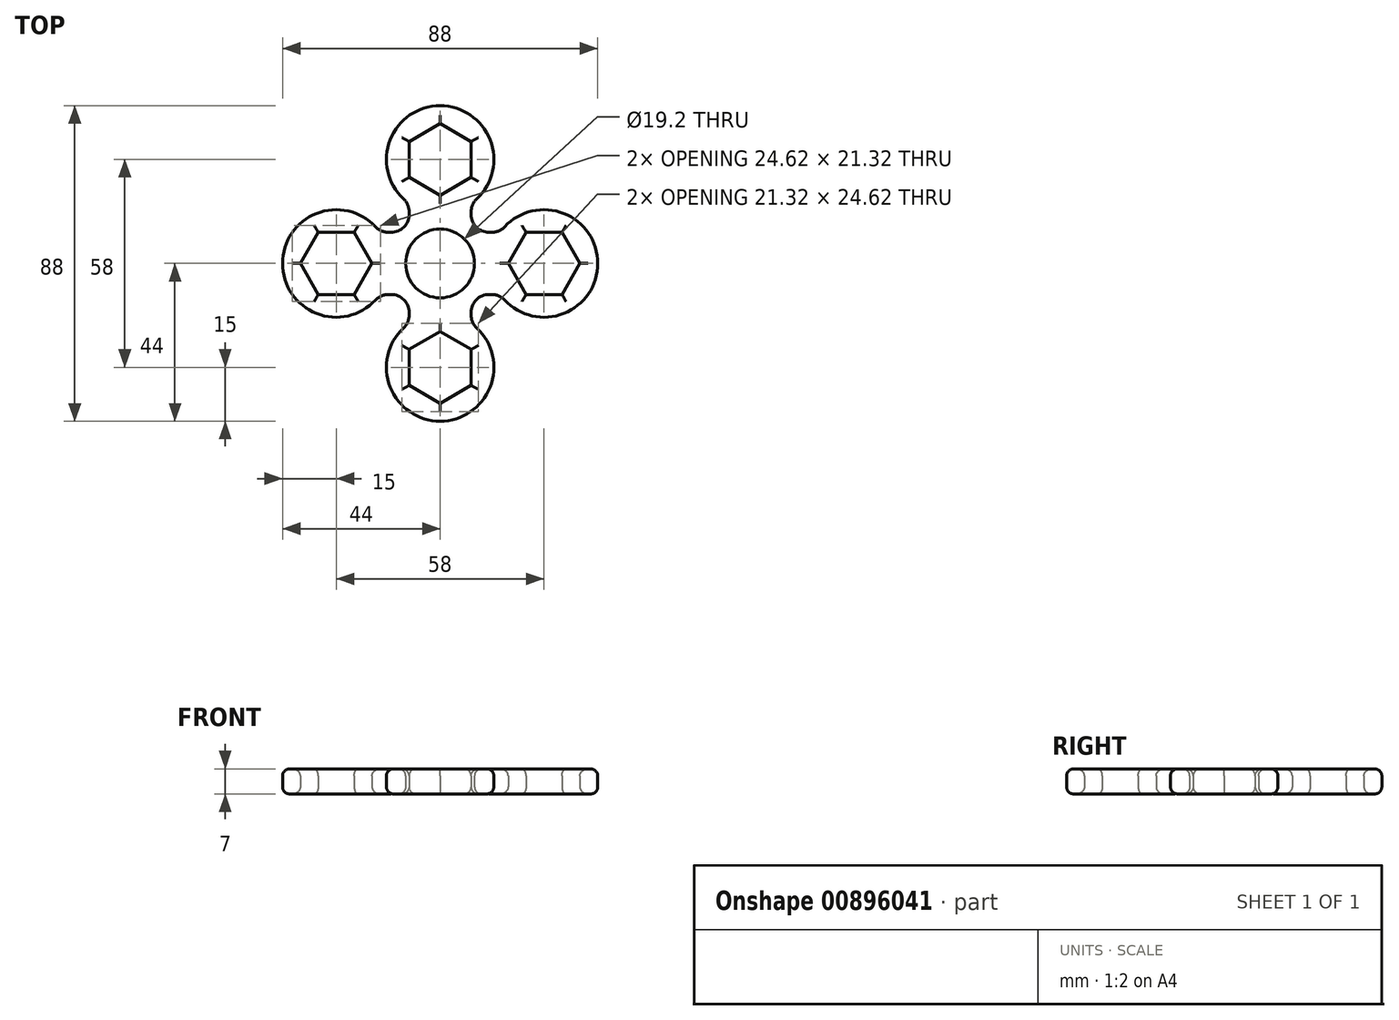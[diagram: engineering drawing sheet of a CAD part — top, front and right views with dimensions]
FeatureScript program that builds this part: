
annotation { "Feature Type Name" : "Feature", "Feature Type Description" : "" }
export const myFeature = defineFeature(function(context is Context, id is Id, definition is map)
    precondition{}
    {
        {
            var Q0;
            Q0=qCreatedBy(makeId("Top.planeOp"),FACE);
            var sketch = newSketch(context, id + "F0", { "sketchPlane" : qUnion([Q0])});
            skCircle(sketch, "E0", {"center": v(0, 0) * mm, "radius": 9.6 * mm});
            skLineSegment(sketch, "E1", {"start": v(0, 8.66) * mm, "end": v(0, 9.6) * mm, "construction": true});
            skLineSegment(sketch, "E2", {"start": v(0, -8.66) * mm, "end": v(0, -9.6) * mm});
            skCircle(sketch, "E3.cCircle", {"center": v(0, 29) * mm, "radius": 8.66 * mm, "construction": true});
            skLineSegment(sketch, "E3.0", {"start": v(8.66, 34) * mm, "end": v(8.66, 24) * mm});
            skLineSegment(sketch, "E3.1", {"start": v(8.66, 24) * mm, "end": v(0, 19) * mm});
            skLineSegment(sketch, "E3.2", {"start": v(0, 19) * mm, "end": v(-8.66, 24) * mm});
            skLineSegment(sketch, "E3.3", {"start": v(-8.66, 24) * mm, "end": v(-8.66, 34) * mm});
            skLineSegment(sketch, "E3.4", {"start": v(-8.66, 34) * mm, "end": v(0, 39) * mm});
            skLineSegment(sketch, "E3.5", {"start": v(0, 39) * mm, "end": v(8.66, 34) * mm});
            skPoint(sketch, "E3.0.midPoint", {"position": v(8.66, 29) * mm});
            skArc(sketch, "E4", {"start": v(10.25, 18.04) * mm, "mid": v(0, 44) * mm, "end": v(-10.25, 18.04) * mm});
            skArc(sketch, "E5.1.0", {"start": v(-18.04, 10.25) * mm, "mid": v(-44, 0) * mm, "end": v(-18.04, -10.25) * mm});
            skLineSegment(sketch, "E5.1.1", {"start": v(-34, -8.66) * mm, "end": v(-39, 0) * mm});
            skLineSegment(sketch, "E5.1.2", {"start": v(-19, 0) * mm, "end": v(-24, -8.66) * mm});
            skLineSegment(sketch, "E5.1.3", {"start": v(-24, 8.66) * mm, "end": v(-19, 0) * mm});
            skLineSegment(sketch, "E5.1.4", {"start": v(-34, 8.66) * mm, "end": v(-24, 8.66) * mm});
            skLineSegment(sketch, "E5.1.5", {"start": v(-39, 0) * mm, "end": v(-34, 8.66) * mm});
            skLineSegment(sketch, "E5.1.6", {"start": v(-24, -8.66) * mm, "end": v(-34, -8.66) * mm});
            skArc(sketch, "E5.2.0", {"start": v(-10.25, -18.04) * mm, "mid": v(0, -44) * mm, "end": v(10.25, -18.04) * mm});
            skLineSegment(sketch, "E5.2.1", {"start": v(8.66, -34) * mm, "end": v(0, -39) * mm});
            skLineSegment(sketch, "E5.2.2", {"start": v(0, -19) * mm, "end": v(8.66, -24) * mm});
            skLineSegment(sketch, "E5.2.3", {"start": v(-8.66, -24) * mm, "end": v(0, -19) * mm});
            skLineSegment(sketch, "E5.2.4", {"start": v(-8.66, -34) * mm, "end": v(-8.66, -24) * mm});
            skLineSegment(sketch, "E5.2.5", {"start": v(0, -39) * mm, "end": v(-8.66, -34) * mm});
            skLineSegment(sketch, "E5.2.6", {"start": v(8.66, -24) * mm, "end": v(8.66, -34) * mm});
            skArc(sketch, "E5.3.0", {"start": v(18.04, -10.25) * mm, "mid": v(44, 0) * mm, "end": v(18.04, 10.25) * mm});
            skLineSegment(sketch, "E5.3.1", {"start": v(34, 8.66) * mm, "end": v(39, 0) * mm});
            skLineSegment(sketch, "E5.3.2", {"start": v(19, 0) * mm, "end": v(24, 8.66) * mm});
            skLineSegment(sketch, "E5.3.3", {"start": v(24, -8.66) * mm, "end": v(19, 0) * mm});
            skLineSegment(sketch, "E5.3.4", {"start": v(34, -8.66) * mm, "end": v(24, -8.66) * mm});
            skLineSegment(sketch, "E5.3.5", {"start": v(39, 0) * mm, "end": v(34, -8.66) * mm});
            skLineSegment(sketch, "E5.3.6", {"start": v(24, 8.66) * mm, "end": v(34, 8.66) * mm});
            skLineSegment(sketch, "E6", {"start": v(-8.66, 14.4) * mm, "end": v(-8.66, 13.66) * mm});
            skLineSegment(sketch, "E7", {"start": v(8.66, 14.4) * mm, "end": v(8.66, 13.66) * mm});
            skLineSegment(sketch, "E8", {"start": v(14.4, 8.66) * mm, "end": v(13.66, 8.66) * mm});
            skLineSegment(sketch, "E9", {"start": v(-14.4, 8.66) * mm, "end": v(-13.66, 8.66) * mm});
            skLineSegment(sketch, "E10", {"start": v(-14.4, -8.66) * mm, "end": v(-13.66, -8.66) * mm});
            skLineSegment(sketch, "E11", {"start": v(14.4, -8.66) * mm, "end": v(13.66, -8.66) * mm});
            skLineSegment(sketch, "E12", {"start": v(-8.66, -14.4) * mm, "end": v(-8.66, -13.66) * mm});
            skLineSegment(sketch, "E13", {"start": v(8.66, -14.4) * mm, "end": v(8.66, -13.66) * mm});
            skLineSegment(sketch, "E14.trimOffspring", {"start": v(0, 19) * mm, "end": v(0, 20.34) * mm, "construction": true});
            skPoint(sketch, "E15.trimOffspring.end.orphan", {"position": v(44, 0) * mm});
            skPoint(sketch, "E16.orphan", {"position": v(0, -8.66) * mm});
            skPoint(sketch, "E17.orphan", {"position": v(0, -44) * mm});
            skLineSegment(sketch, "E18.trimOffspring", {"start": v(0, -19) * mm, "end": v(0, -39) * mm});
            skLineSegment(sketch, "E19.trimOffspring", {"start": v(0, 37.66) * mm, "end": v(0, 44) * mm, "construction": true});
            skPoint(sketch, "E20.visualSharp", {"position": v(-8.66, 8.66) * mm});
            skArc(sketch, "E20.filletArc", {"start": v(-13.66, 8.66) * mm, "mid": v(-10.12, 10.12) * mm, "end": v(-8.66, 13.66) * mm});
            skPoint(sketch, "E21.visualSharp", {"position": v(8.66, 8.66) * mm});
            skArc(sketch, "E21.filletArc", {"start": v(8.66, 13.66) * mm, "mid": v(10.12, 10.12) * mm, "end": v(13.66, 8.66) * mm});
            skPoint(sketch, "E22.visualSharp", {"position": v(8.66, -8.66) * mm});
            skArc(sketch, "E22.filletArc", {"start": v(13.66, -8.66) * mm, "mid": v(10.12, -10.12) * mm, "end": v(8.66, -13.66) * mm});
            skPoint(sketch, "E23.visualSharp", {"position": v(-8.66, -8.66) * mm});
            skArc(sketch, "E23.filletArc", {"start": v(-8.66, -13.66) * mm, "mid": v(-10.12, -10.12) * mm, "end": v(-13.66, -8.66) * mm});
            skPoint(sketch, "E24.visualSharp", {"position": v(-8.66, -16.75) * mm});
            skArc(sketch, "E24.filletArc", {"start": v(-10.25, -18.04) * mm, "mid": v(-9.07, -16.38) * mm, "end": v(-8.66, -14.4) * mm});
            skPoint(sketch, "E25.visualSharp", {"position": v(8.66, -16.75) * mm});
            skArc(sketch, "E25.filletArc", {"start": v(8.66, -14.4) * mm, "mid": v(9.07, -16.38) * mm, "end": v(10.25, -18.04) * mm});
            skPoint(sketch, "E26.visualSharp", {"position": v(16.75, -8.66) * mm});
            skArc(sketch, "E26.filletArc", {"start": v(18.04, -10.25) * mm, "mid": v(16.38, -9.07) * mm, "end": v(14.4, -8.66) * mm});
            skPoint(sketch, "E27.visualSharp", {"position": v(-16.75, -8.66) * mm});
            skArc(sketch, "E27.filletArc", {"start": v(-14.4, -8.66) * mm, "mid": v(-16.38, -9.07) * mm, "end": v(-18.04, -10.25) * mm});
            skPoint(sketch, "E28.visualSharp", {"position": v(-16.75, 8.66) * mm});
            skArc(sketch, "E28.filletArc", {"start": v(-18.04, 10.25) * mm, "mid": v(-16.38, 9.07) * mm, "end": v(-14.4, 8.66) * mm});
            skPoint(sketch, "E29.visualSharp", {"position": v(-8.66, 16.75) * mm});
            skArc(sketch, "E29.filletArc", {"start": v(-8.66, 14.4) * mm, "mid": v(-9.07, 16.38) * mm, "end": v(-10.25, 18.04) * mm});
            skPoint(sketch, "E30.visualSharp", {"position": v(8.66, 16.75) * mm});
            skArc(sketch, "E30.filletArc", {"start": v(10.25, 18.04) * mm, "mid": v(9.07, 16.38) * mm, "end": v(8.66, 14.4) * mm});
            skPoint(sketch, "E31.visualSharp", {"position": v(16.75, 8.66) * mm});
            skArc(sketch, "E31.filletArc", {"start": v(14.4, 8.66) * mm, "mid": v(16.38, 9.07) * mm, "end": v(18.04, 10.25) * mm});
            skSolve(sketch);
        }
        {
            var Q0;
            Q0 = qSketchRegion(id + "F0", true);
            extrude(context, id + "F1", {"entities" : qUnion([Q0]), "depth" : 7 * mm, "offsetDistance" : 25 * mm});
        }
        {
            var Q0;
            Q0=makeQuery(id+"F1.opExtrude","CAP_FACE",FACE,{"disambiguationData":[OSD([sQuery(id+"F0.wireOp",EDGE,"E0"),sQuery(id+"F0.wireOp",EDGE,"E3.0"),sQuery(id+"F0.wireOp",EDGE,"E3.1"),sQuery(id+"F0.wireOp",EDGE,"E3.2"),sQuery(id+"F0.wireOp",EDGE,"E3.3"),sQuery(id+"F0.wireOp",EDGE,"E3.4"),sQuery(id+"F0.wireOp",EDGE,"E3.5"),sQuery(id+"F0.wireOp",EDGE,"E4"),sQuery(id+"F0.wireOp",EDGE,"E5.1.0"),sQuery(id+"F0.wireOp",EDGE,"E5.1.1"),sQuery(id+"F0.wireOp",EDGE,"E5.1.2"),sQuery(id+"F0.wireOp",EDGE,"E5.1.3"),sQuery(id+"F0.wireOp",EDGE,"E5.1.4"),sQuery(id+"F0.wireOp",EDGE,"E5.1.5"),sQuery(id+"F0.wireOp",EDGE,"E5.1.6"),sQuery(id+"F0.wireOp",EDGE,"E5.2.0"),sQuery(id+"F0.wireOp",EDGE,"E5.2.1"),sQuery(id+"F0.wireOp",EDGE,"E5.2.2"),sQuery(id+"F0.wireOp",EDGE,"E5.2.3"),sQuery(id+"F0.wireOp",EDGE,"E5.2.4"),sQuery(id+"F0.wireOp",EDGE,"E5.2.5"),sQuery(id+"F0.wireOp",EDGE,"E5.2.6"),sQuery(id+"F0.wireOp",EDGE,"E5.3.0"),sQuery(id+"F0.wireOp",EDGE,"E5.3.1"),sQuery(id+"F0.wireOp",EDGE,"E5.3.2"),sQuery(id+"F0.wireOp",EDGE,"E5.3.3"),sQuery(id+"F0.wireOp",EDGE,"E5.3.4"),sQuery(id+"F0.wireOp",EDGE,"E5.3.5"),sQuery(id+"F0.wireOp",EDGE,"E5.3.6"),sQuery(id+"F0.wireOp",EDGE,"E6"),sQuery(id+"F0.wireOp",EDGE,"E7"),sQuery(id+"F0.wireOp",EDGE,"E8"),sQuery(id+"F0.wireOp",EDGE,"E9"),sQuery(id+"F0.wireOp",EDGE,"E10"),sQuery(id+"F0.wireOp",EDGE,"E11"),sQuery(id+"F0.wireOp",EDGE,"E12"),sQuery(id+"F0.wireOp",EDGE,"E13"),sQuery(id+"F0.wireOp",EDGE,"E20.filletArc"),sQuery(id+"F0.wireOp",EDGE,"E21.filletArc"),sQuery(id+"F0.wireOp",EDGE,"E22.filletArc"),sQuery(id+"F0.wireOp",EDGE,"E23.filletArc"),sQuery(id+"F0.wireOp",EDGE,"E24.filletArc"),sQuery(id+"F0.wireOp",EDGE,"E25.filletArc"),sQuery(id+"F0.wireOp",EDGE,"E26.filletArc"),sQuery(id+"F0.wireOp",EDGE,"E27.filletArc"),sQuery(id+"F0.wireOp",EDGE,"E28.filletArc"),sQuery(id+"F0.wireOp",EDGE,"E29.filletArc"),sQuery(id+"F0.wireOp",EDGE,"E30.filletArc"),sQuery(id+"F0.wireOp",EDGE,"E31.filletArc")])],"isStart":false});
            fillet(context, id + "F2", {"entities" : qUnion([Q0]), "radius" : 2 * mm, "tangentPropagation" : true, "allowEdgeOverflow" : false});
        }
        {
            var Q0;
            Q0=makeQuery(id+"F1.opExtrude","CAP_FACE",FACE,{"disambiguationData":[OSD([sQuery(id+"F0.wireOp",EDGE,"E0"),sQuery(id+"F0.wireOp",EDGE,"E3.0"),sQuery(id+"F0.wireOp",EDGE,"E3.1"),sQuery(id+"F0.wireOp",EDGE,"E3.2"),sQuery(id+"F0.wireOp",EDGE,"E3.3"),sQuery(id+"F0.wireOp",EDGE,"E3.4"),sQuery(id+"F0.wireOp",EDGE,"E3.5"),sQuery(id+"F0.wireOp",EDGE,"E4"),sQuery(id+"F0.wireOp",EDGE,"E5.1.0"),sQuery(id+"F0.wireOp",EDGE,"E5.1.1"),sQuery(id+"F0.wireOp",EDGE,"E5.1.2"),sQuery(id+"F0.wireOp",EDGE,"E5.1.3"),sQuery(id+"F0.wireOp",EDGE,"E5.1.4"),sQuery(id+"F0.wireOp",EDGE,"E5.1.5"),sQuery(id+"F0.wireOp",EDGE,"E5.1.6"),sQuery(id+"F0.wireOp",EDGE,"E5.2.0"),sQuery(id+"F0.wireOp",EDGE,"E5.2.1"),sQuery(id+"F0.wireOp",EDGE,"E5.2.2"),sQuery(id+"F0.wireOp",EDGE,"E5.2.3"),sQuery(id+"F0.wireOp",EDGE,"E5.2.4"),sQuery(id+"F0.wireOp",EDGE,"E5.2.5"),sQuery(id+"F0.wireOp",EDGE,"E5.2.6"),sQuery(id+"F0.wireOp",EDGE,"E5.3.0"),sQuery(id+"F0.wireOp",EDGE,"E5.3.1"),sQuery(id+"F0.wireOp",EDGE,"E5.3.2"),sQuery(id+"F0.wireOp",EDGE,"E5.3.3"),sQuery(id+"F0.wireOp",EDGE,"E5.3.4"),sQuery(id+"F0.wireOp",EDGE,"E5.3.5"),sQuery(id+"F0.wireOp",EDGE,"E5.3.6"),sQuery(id+"F0.wireOp",EDGE,"E6"),sQuery(id+"F0.wireOp",EDGE,"E7"),sQuery(id+"F0.wireOp",EDGE,"E8"),sQuery(id+"F0.wireOp",EDGE,"E9"),sQuery(id+"F0.wireOp",EDGE,"E10"),sQuery(id+"F0.wireOp",EDGE,"E11"),sQuery(id+"F0.wireOp",EDGE,"E12"),sQuery(id+"F0.wireOp",EDGE,"E13"),sQuery(id+"F0.wireOp",EDGE,"E20.filletArc"),sQuery(id+"F0.wireOp",EDGE,"E21.filletArc"),sQuery(id+"F0.wireOp",EDGE,"E22.filletArc"),sQuery(id+"F0.wireOp",EDGE,"E23.filletArc"),sQuery(id+"F0.wireOp",EDGE,"E24.filletArc"),sQuery(id+"F0.wireOp",EDGE,"E25.filletArc"),sQuery(id+"F0.wireOp",EDGE,"E26.filletArc"),sQuery(id+"F0.wireOp",EDGE,"E27.filletArc"),sQuery(id+"F0.wireOp",EDGE,"E28.filletArc"),sQuery(id+"F0.wireOp",EDGE,"E29.filletArc"),sQuery(id+"F0.wireOp",EDGE,"E30.filletArc"),sQuery(id+"F0.wireOp",EDGE,"E31.filletArc")])],"isStart":true});
            fillet(context, id + "F3", {"entities" : qUnion([Q0]), "radius" : 2 * mm, "tangentPropagation" : true, "allowEdgeOverflow" : false});
        }
    });
